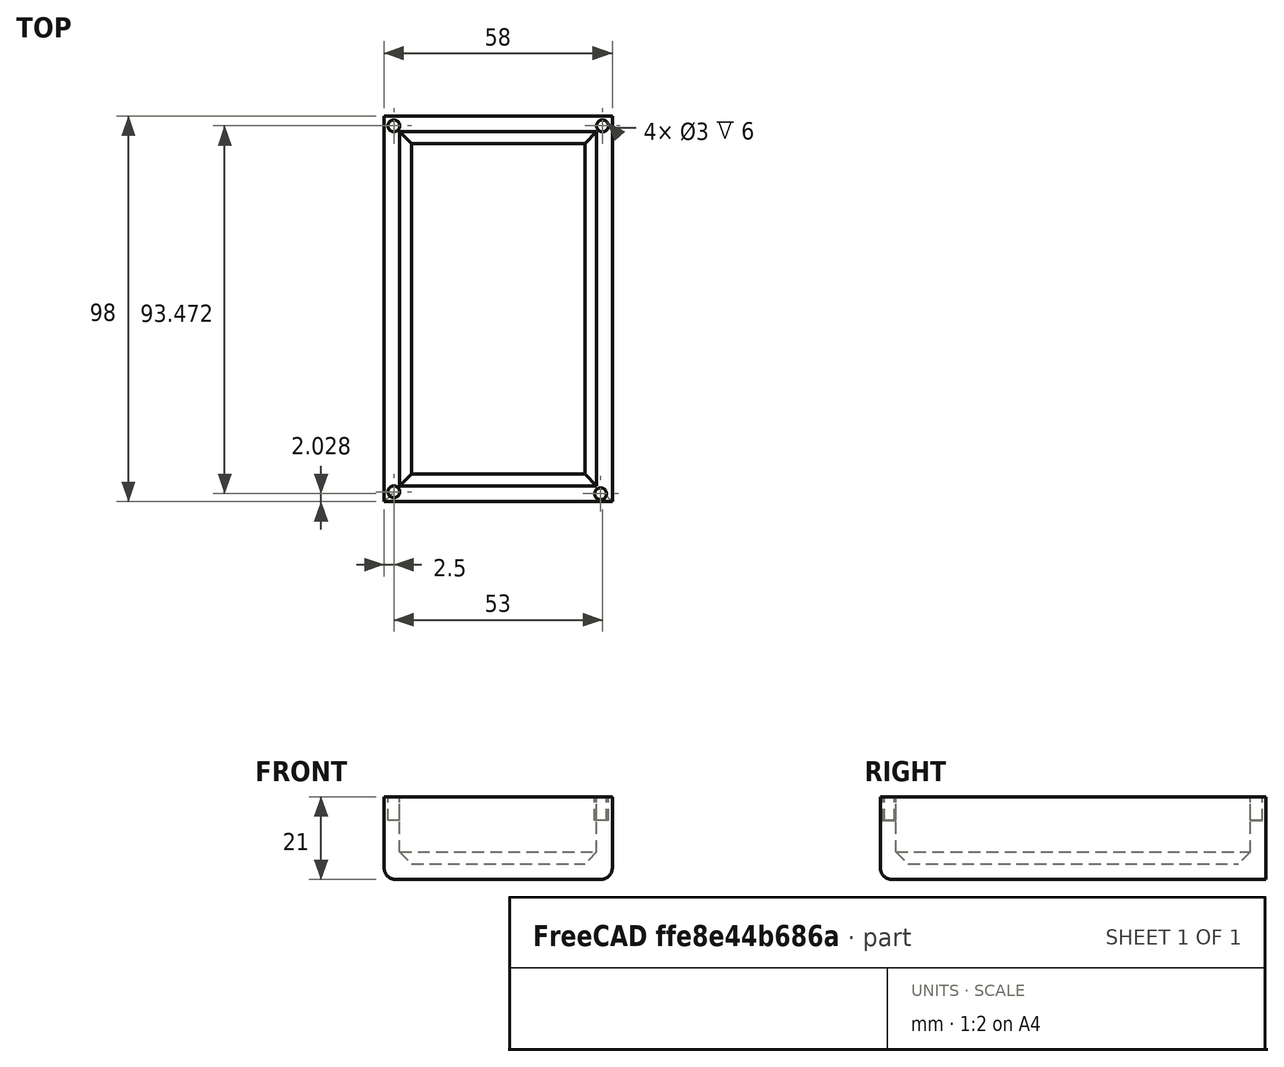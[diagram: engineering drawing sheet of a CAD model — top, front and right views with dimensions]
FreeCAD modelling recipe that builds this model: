
FCSTD DOCUMENT  (FreeCAD 0.17R13541 (Git))
Label: LifelineCase_Top
License: All rights reserved
LicenseURL: http://en.wikipedia.org/wiki/All_rights_reserved
objects: Part::Cut×5, Part::Cylinder×4, Part::Box×2, Part::Chamfer×1, Part::Fillet×1
note: 13 computed .brp shape members not serialized (recipe doc carries the construction recipe); baked Part::Feature solids carry a one-line shape summary decoded from their .brp

FEATURE [Part::Box] Box  label="Case"
  AttacherType = Attacher::AttachEngine3D
  Height = 21
  Length = 58
  Width = 98
FEATURE [Part::Cylinder] Cylinder002
  Angle = 360
  AttacherType = Attacher::AttachEngine3D
  Height = 6
  Placement = pos=(2.5,95.5,15) rot=(0,0,1;0rad)
  Radius = 1.5
FEATURE [Part::Box] Box001  label="Cutout"
  AttacherType = Attacher::AttachEngine3D
  Height = 17
  Length = 50
  Placement = pos=(4,4,4) rot=(0,0,1;0rad)
  Width = 90
FEATURE [Part::Chamfer] Chamfer
  Base = -> Box001
  Edges = 4 edges r=3: [Edge4,Edge8,Edge9,Edge11]
FEATURE [Part::Cut] Cut
  Base = -> Box
  Tool = -> Chamfer
FEATURE [Part::Fillet] Fillet
  Base = -> Cut
  Edges = 3 edges r=3: [Edge4,Edge5,Edge16]
FEATURE [Part::Cylinder] Cylinder001
  Angle = 360
  AttacherType = Attacher::AttachEngine3D
  Height = 6
  Placement = pos=(55.012,2.02785,15) rot=(0,0,1;0rad)
  Radius = 1.5
FEATURE [Part::Cylinder] Cylinder003
  Angle = 360
  AttacherType = Attacher::AttachEngine3D
  Height = 6
  Placement = pos=(55.5,95.5,15) rot=(0,0,1;0rad)
  Radius = 1.5
FEATURE [Part::Cylinder] Cylinder
  Angle = 360
  AttacherType = Attacher::AttachEngine3D
  Height = 6
  Placement = pos=(2.5,2.5,15) rot=(0,0,1;0rad)
  Radius = 1.5
FEATURE [Part::Cut] Cut001
  Base = -> Fillet
  Tool = -> Cylinder
FEATURE [Part::Cut] Cut002
  Base = -> Cut001
  Tool = -> Cylinder002
FEATURE [Part::Cut] Cut003
  Base = -> Cut002
  Tool = -> Cylinder001
FEATURE [Part::Cut] Cut004  label="Case_Top"
  Base = -> Cut003
  Tool = -> Cylinder003
